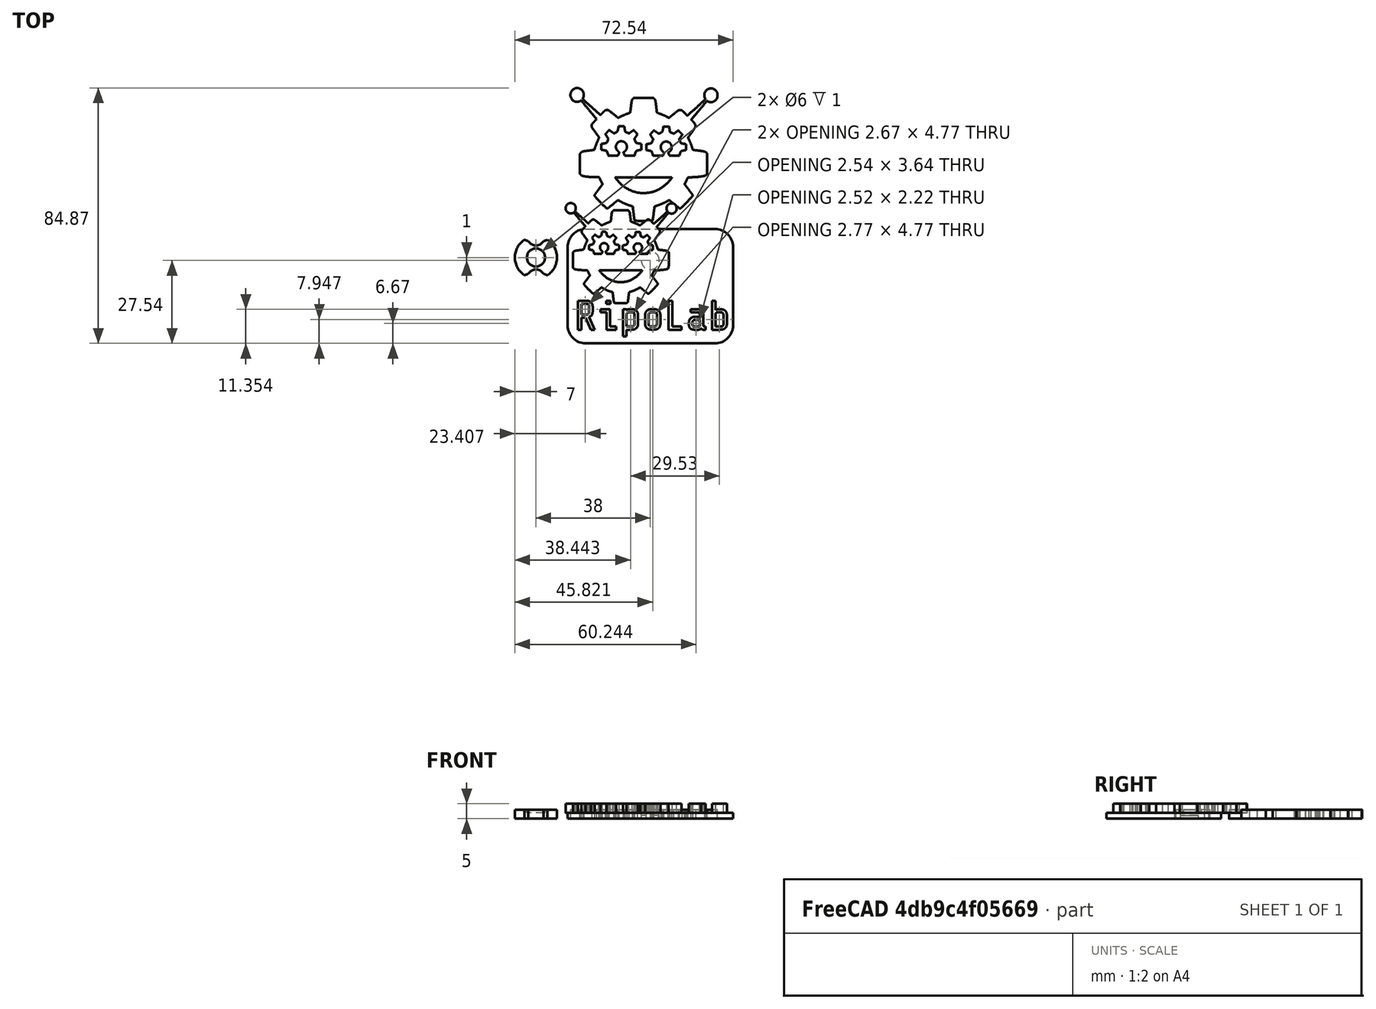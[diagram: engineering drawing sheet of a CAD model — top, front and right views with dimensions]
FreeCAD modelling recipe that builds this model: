
FCSTD DOCUMENT  (FreeCAD 0.16R)
Label: pin_3d
License: All rights reserved
LicenseURL: http://es.wikipedia.org/wiki/Todos_los_derechos_reservados
objects: Part::Feature×6, Part::Cut×6, Part::FeaturePython×6, Part::Cylinder×5, Part::Extrusion×4, Part::MultiFuse×1, Part::Part2DObjectPython×1, Part::Box×1, Part::Fillet×1, Part::Chamfer×1
note: 32 computed .brp shape members not serialized (recipe doc carries the construction recipe); baked Part::Feature solids carry a one-line shape summary decoded from their .brp

FEATURE [Part::Feature] path3415
  Placement = pos=(0,659.362,0) rot=(0,0,1;0rad)
  shape: bbox 117.4 x 51.57 x 2e-07 mm, 1 faces, 0 solids (baked)
FEATURE [Part::Feature] path3415001
  Placement = pos=(0,652.362,0) rot=(0,0,1;0rad)
  shape: bbox 176.2 x 103.8 x 2e-07 mm, 1 faces, 0 solids (baked)
FEATURE [Part::Feature] path3415002
  Placement = pos=(0,652.362,0) rot=(0,0,1;0rad)
  shape: bbox 47.84 x 42.86 x 2e-07 mm, 1 faces, 0 solids (baked)
FEATURE [Part::Feature] path3415003
  Placement = pos=(0,652.362,0) rot=(0,0,1;0rad)
  shape: bbox 47.84 x 42.86 x 2e-07 mm, 1 faces, 0 solids (baked)
FEATURE [Part::Feature] rect3550
  Placement = pos=(0,652.362,0) rot=(0,0,1;0rad)
  shape: bbox 106.5 x 12.59 x 2e-07 mm, 1 faces, 0 solids (baked)
FEATURE [Part::Cut] Cut
  Base = -> path3415001
  Tool = -> path3415002
FEATURE [Part::Cut] Cut001
  Base = -> Cut
  Tool = -> path3415003
FEATURE [Part::MultiFuse] Fusion
  Shapes = -> [rect3550,path3415,Cut001]
FEATURE [Part::Feature] Fusion001
  shape: bbox 176.2 x 154.3 x 2e-07 mm, 1 faces, 0 solids (baked)
FEATURE [Part::FeaturePython] Scale  # Draft clone (typed FeaturePython)
  Objects = -> [Fusion001]
  Placement = pos=(206.467,-13.441,0) rot=(0,0,1;0rad)
  Scale = (-0.207174,0.408746,1)
FEATURE [Part::FeaturePython] Scale001  # Draft clone (typed FeaturePython)
  Objects = -> [Scale]
  Placement = pos=(625.973,11.3276,0) rot=(0,0,1;0rad)
  Scale = (-2.62938,1.43578,1)
FEATURE [Part::FeaturePython] Scale002  # Draft clone (typed FeaturePython)
  Objects = -> [Scale001]
  Placement = pos=(728.448,74.9706,0) rot=(0,0,1;0rad)
  Scale = (0.658762,0.658762,1)
FEATURE [Part::FeaturePython] Scale003  # Draft clone (typed FeaturePython)
  Objects = -> [Scale002]
  Placement = pos=(729.68,133.895,0) rot=(0,0,1;0rad)
  Scale = (0.160579,-0.160579,1)
FEATURE [Part::FeaturePython] Scale004  # Draft clone (typed FeaturePython)
  Objects = -> [Scale003]
  Placement = pos=(713.323,357.471,0) rot=(0,0,1;0rad)
  Scale = (3.17855,-3.05375,1)
FEATURE [Part::Extrusion] Extrude
  Base = -> Scale004
  Dir = (0,0,3)
  Solid = false
FEATURE [Part::Extrusion] Extrude001
  Base = -> Scale004
  Dir = (0,0,3)
  Solid = false
FEATURE [Part::Extrusion] Extrude002
  Base = -> Scale004
  Dir = (0,0,3)
  Placement = pos=(0,-48,2) rot=(0,0,1;0rad)
  Solid = false
FEATURE [Part::FeaturePython] Scale005  label="cara logo"  # Draft clone (typed FeaturePython)
  Objects = -> [Extrude002]
  Placement = pos=(-7.12577,64.0289,2) rot=(0,0,1;3.14159rad)
  Scale = (-0.753602,-0.753602,1)
FEATURE [Part::Part2DObjectPython] ShapeString  # Draft 2D object (typed FeaturePython)
  FontFile = <userpath>/devs/ripolab/fonts/Share_Tech_Mono/ShareTechMono-Regular.ttf
  Placement = pos=(-30,-6,0) rot=(0,0,1;0rad)
  Size = 5
  String = RipoLab
  Tracking = 0
FEATURE [Part::Extrusion] Extrude003  label="texto RIPOLAB"
  Base = -> ShapeString
  Dir = (0,0,3)
  Placement = pos=(9,-1,2) rot=(0,0,1;0rad)
  Solid = true
FEATURE [Part::Box] Box  label="Cubo"
  Height = 2
  Length = 55
  Placement = pos=(-23.4593,-11.5423,0) rot=(0,0,1;0rad)
  Width = 38
FEATURE [Part::Fillet] Fillet
  Base = -> Box
  Edges = 4 edges r=6: [Edge1,Edge3,Edge5,Edge7]
FEATURE [Part::Cylinder] Cylinder  label="Cilindro"
  Angle = 360
  Height = 1
  Placement = pos=(4,16,0) rot=(0,0,1;0rad)
  Radius = 3
FEATURE [Part::Cut] Cut002
  Base = -> Fillet
  Tool = -> Cylinder
FEATURE [Part::Cylinder] Cylinder001  label="Cilindro001"
  Angle = 360
  Height = 1
  Placement = pos=(4,16,-1) rot=(0,0,1;0rad)
  Radius = 3
FEATURE [Part::Cylinder] Cylinder002  label="Cilindro002"
  Angle = 360
  Height = 3
  Placement = pos=(4,16,-3) rot=(0,0,1;0rad)
  Radius = 7
FEATURE [Part::Cylinder] Cylinder003  label="Cilindro003"
  Angle = 360
  Height = 3
  Placement = pos=(4,23,-3) rot=(0,0,1;0rad)
  Radius = 3
FEATURE [Part::Cylinder] Cylinder004  label="Cilindro004"
  Angle = 360
  Height = 3
  Placement = pos=(4,9,-3) rot=(0,0,1;0rad)
  Radius = 3
FEATURE [Part::Cut] Cut003
  Base = -> Cylinder002
  Tool = -> Cylinder003
FEATURE [Part::Cut] Cut004
  Base = -> Cut003
  Tool = -> Cylinder004
FEATURE [Part::Cut] Cut005
  Base = -> Cut004
  Tool = -> Cylinder001
FEATURE [Part::Chamfer] Chamfer
  Base = -> Cut005
  Edges = 4 edges r=1: [Edge7,Edge8,Edge9,Edge13]
  Placement = pos=(-38,1,3) rot=(0,0,1;0rad)
